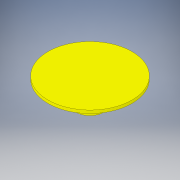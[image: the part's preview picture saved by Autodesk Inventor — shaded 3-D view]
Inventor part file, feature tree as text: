
AUTODESK INVENTOR PART (.ipt)
format: ipt  version: 2019 (Build 230136000, 136)  size: 127,488 bytes
history: native  units: mm
features: extrude x4, sketch x4
ambient origin geometry x8: Origin, YZ Plane, XZ Plane, XY Plane, X Axis, Y Axis, Z Axis, Center Point
bodies: Solid1 (feature_tree)
feature tree (8):
  extrude  "Extrusion1"  Depth=20.0mm TaperAngle=0.0deg
  extrude  "Extrusion2"  Depth=3.18mm TaperAngle=0.0deg
  extrude  "Extrusion3"  Depth=3.18mm TaperAngle=0.0deg
  extrude  "Extrusion4"  Depth=3.18mm TaperAngle=0.0deg
  sketch  "Sketch1"  dims[d0=10.0mm d1=20.0mm d2=0.0mm]
  sketch  "Sketch2"  dims[d3=90.0mm d4=3.18mm d5=0.0mm]
  sketch  "Sketch3"  dims[d6=30.0mm d7=3.18mm d8=0.0mm]
  sketch  "Sketch4"  dims[d9=12.0mm d10=3.18mm d11=0.0mm]
